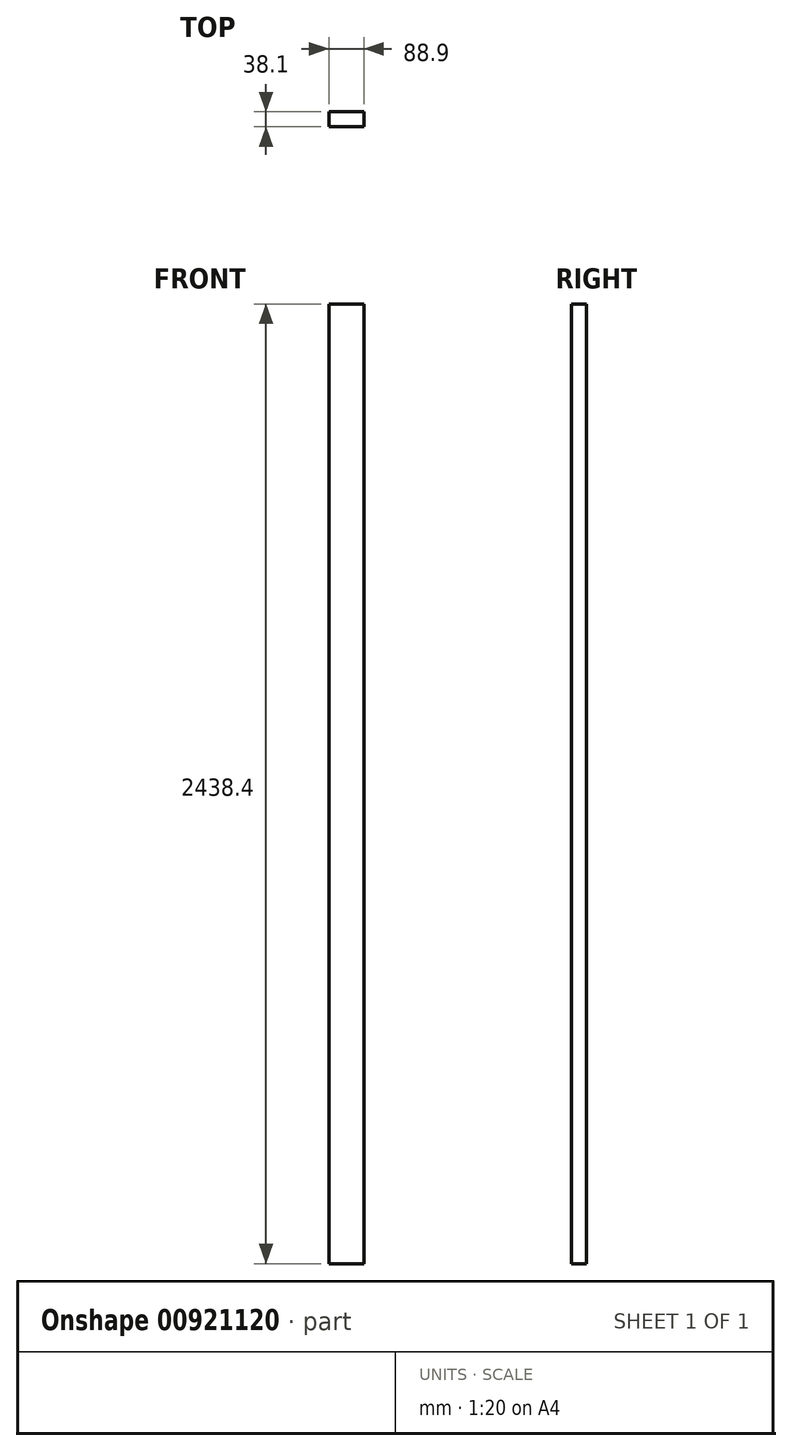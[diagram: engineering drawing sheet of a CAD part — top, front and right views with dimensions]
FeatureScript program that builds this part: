
annotation { "Feature Type Name" : "Feature", "Feature Type Description" : "" }
export const myFeature = defineFeature(function(context is Context, id is Id, definition is map)
    precondition{}
    {
        {
            var Q0;
            Q0=qCreatedBy(makeId("Top.planeOp"),FACE);
            var sketch = newSketch(context, id + "F0", { "sketchPlane" : qUnion([Q0])});
            skLineSegment(sketch, "E0.bottom", {"start": v(0, 0) * mm, "end": v(88.9, 0) * mm});
            skLineSegment(sketch, "E0.top", {"start": v(0, -38.1) * mm, "end": v(88.9, -38.1) * mm});
            skLineSegment(sketch, "E0.left", {"start": v(0, 0) * mm, "end": v(0, -38.1) * mm});
            skLineSegment(sketch, "E0.right", {"start": v(88.9, 0) * mm, "end": v(88.9, -38.1) * mm});
            skSolve(sketch);
        }
        {
            var Q0;
            Q0=makeQuery(id+"F0.imprint","IMPRINT",FACE,{"disambiguationData":[TD([[makeQuery(id+"F0.imprint","IMPRINT",EDGE,{"derivedFrom":sQuery(id+"F0.wireOp",EDGE,"E0.bottom")}),-1.0]])]});
            extrude(context, id + "F1", {"entities" : qUnion([Q0]), "depth" : 2438.4 * mm, "offsetDistance" : 25.4 * mm});
        }
    });
